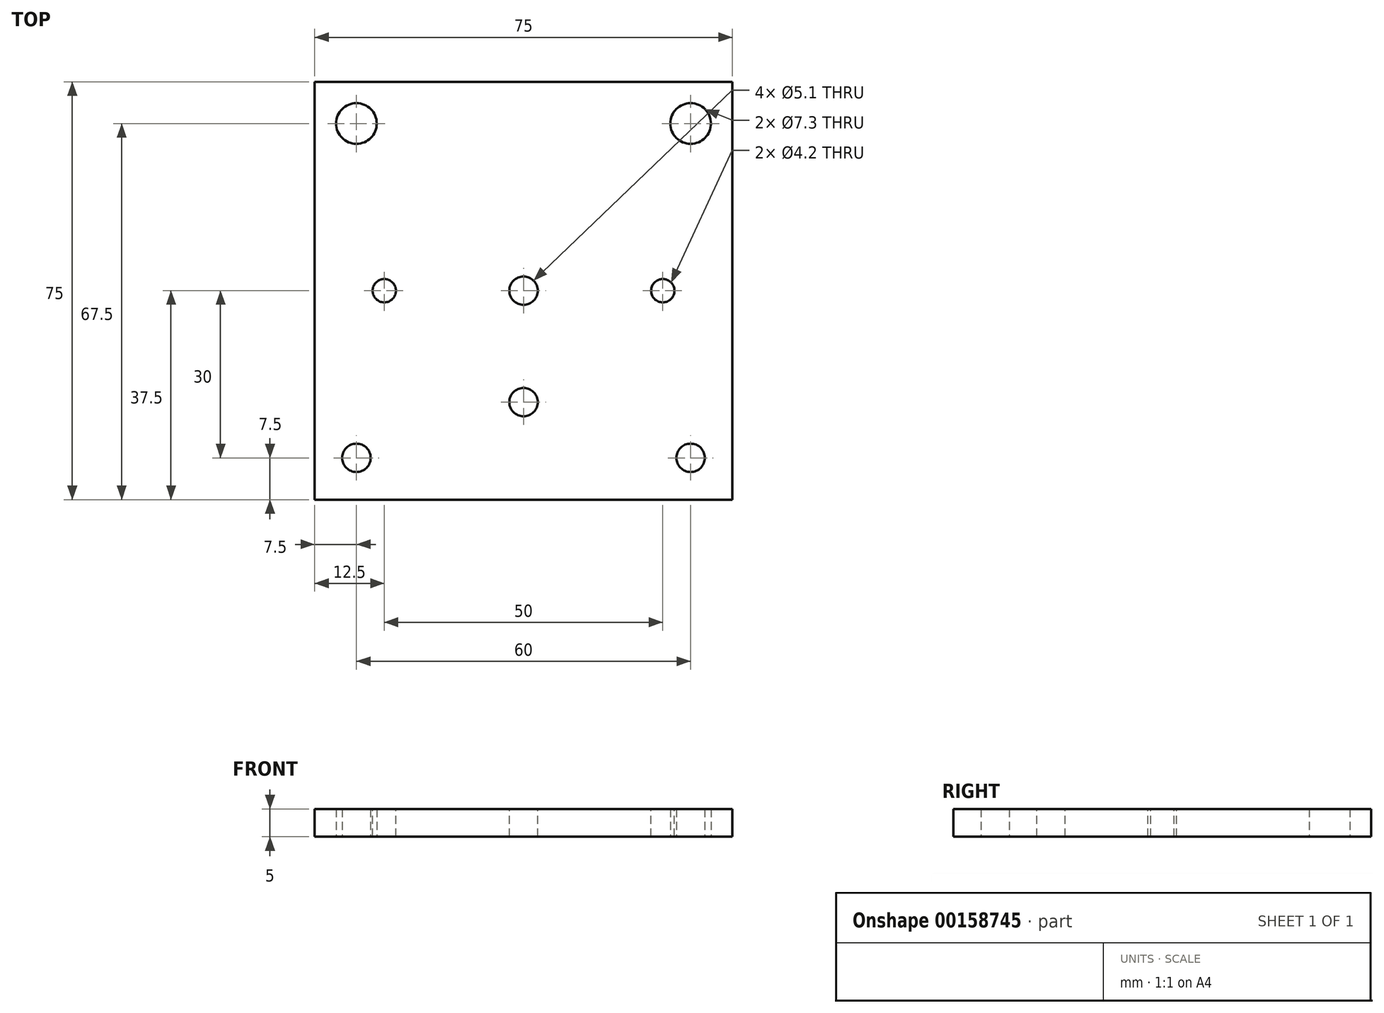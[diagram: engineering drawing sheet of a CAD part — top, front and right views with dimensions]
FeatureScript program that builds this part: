
annotation { "Feature Type Name" : "Feature", "Feature Type Description" : "" }
export const myFeature = defineFeature(function(context is Context, id is Id, definition is map)
    precondition{}
    {
        {
            var Q0;
            Q0=qCreatedBy(makeId("Top.planeOp"),FACE);
            var sketch = newSketch(context, id + "F3", { "sketchPlane" : qUnion([Q0])});
            skLineSegment(sketch, "E0.bottom", {"start": v(30, -30) * mm, "end": v(-30, -30) * mm});
            skLineSegment(sketch, "E0.top", {"start": v(30, 30) * mm, "end": v(-30, 30) * mm});
            skLineSegment(sketch, "E0.left", {"start": v(30, -30) * mm, "end": v(30, 30) * mm});
            skLineSegment(sketch, "E0.right", {"start": v(-30, -30) * mm, "end": v(-30, 30) * mm});
            skPoint(sketch, "E0.middle", {"position": v(0, 0) * mm});
            skLineSegment(sketch, "E1.bottom", {"start": v(37.5, -37.5) * mm, "end": v(-37.5, -37.5) * mm});
            skLineSegment(sketch, "E1.top", {"start": v(37.5, 37.5) * mm, "end": v(-37.5, 37.5) * mm});
            skLineSegment(sketch, "E1.left", {"start": v(37.5, -37.5) * mm, "end": v(37.5, 37.5) * mm});
            skLineSegment(sketch, "E1.right", {"start": v(-37.5, -37.5) * mm, "end": v(-37.5, 37.5) * mm});
            skSolve(sketch);
        }
        {
            var Q0;
            Q0=makeQuery(id+"F3.imprint","IMPRINT",FACE,{"disambiguationData":[TD([[makeQuery(id+"F3.imprint","IMPRINT",EDGE,{"derivedFrom":sQuery(id+"F3.wireOp",EDGE,"E0.bottom")}),-1.0]])]});
            var Q1;
            Q1=makeQuery(id+"F3.imprint","IMPRINT",FACE,{"disambiguationData":[TD([[makeQuery(id+"F3.imprint","IMPRINT",EDGE,{"derivedFrom":sQuery(id+"F3.wireOp",EDGE,"E0.bottom")}),1.0]])]});
            extrude(context, id + "F4", {"entities" : qUnion([Q0, Q1]), "depth" : 5 * mm});
        }
        {
            var Q0;
            Q0=sQuery(id+"F3.wireOp",VERTEX,"E0.bottom.end");
            var Q1;
            Q1=sQuery(id+"F3.wireOp",VERTEX,"E0.left.start");
            var Q2;
            Q2=makeQuery(id+"F4.opExtrude","SWEPT_BODY",BODY,{"disambiguationData":[OSD([sQuery(id+"F3.wireOp",EDGE,"E1.bottom"),sQuery(id+"F3.wireOp",EDGE,"E1.top"),sQuery(id+"F3.wireOp",EDGE,"E1.left"),sQuery(id+"F3.wireOp",EDGE,"E1.right")])]});
            hole(context, id + "F5", {"style" : HoleStyle.SIMPLE, "endStyle" : HoleEndStyle.THROUGH, "oppositeDirection" : true, "holeDiameter" : 5.1 * mm, "locations" : qUnion([Q0, Q1]), "scope" : qUnion([Q2]), "isTappedThrough" : true});
        }
        {
            var Q0;
            Q0=sQuery(id+"F3.wireOp",VERTEX,"E0.right.end");
            var Q1;
            Q1=sQuery(id+"F3.wireOp",VERTEX,"E0.left.end");
            var Q2;
            Q2=makeQuery(id+"F4.opExtrude","SWEPT_BODY",BODY,{"disambiguationData":[OSD([sQuery(id+"F3.wireOp",EDGE,"E1.bottom"),sQuery(id+"F3.wireOp",EDGE,"E1.top"),sQuery(id+"F3.wireOp",EDGE,"E1.left"),sQuery(id+"F3.wireOp",EDGE,"E1.right")])]});
            hole(context, id + "F0", {"style" : HoleStyle.SIMPLE, "endStyle" : HoleEndStyle.THROUGH, "oppositeDirection" : true, "holeDiameter" : 7.3 * mm, "locations" : qUnion([Q0, Q1]), "scope" : qUnion([Q2]), "isTappedThrough" : true});
        }
        {
            var Q0;
            Q0=makeQuery(id+"F4.opExtrude","CAP_FACE",FACE,{"disambiguationData":[OSD([sQuery(id+"F3.wireOp",EDGE,"E1.bottom"),sQuery(id+"F3.wireOp",EDGE,"E1.top"),sQuery(id+"F3.wireOp",EDGE,"E1.left"),sQuery(id+"F3.wireOp",EDGE,"E1.right")])],"isStart":false});
            var sketch = newSketch(context, id + "F6", { "sketchPlane" : qUnion([Q0])});
            skLineSegment(sketch, "E2", {"start": v(0, 0) * mm, "end": v(0, -20) * mm});
            skSolve(sketch);
        }
        {
            var Q0;
            Q0=sQuery(id+"F6.wireOp",VERTEX,"E2.start");
            var Q1;
            Q1=sQuery(id+"F6.wireOp",VERTEX,"E2.end");
            var Q2;
            Q2=makeQuery(id+"F4.opExtrude","SWEPT_BODY",BODY,{"disambiguationData":[OSD([sQuery(id+"F3.wireOp",EDGE,"E1.bottom"),sQuery(id+"F3.wireOp",EDGE,"E1.top"),sQuery(id+"F3.wireOp",EDGE,"E1.left"),sQuery(id+"F3.wireOp",EDGE,"E1.right")])]});
            hole(context, id + "F1", {"style" : HoleStyle.SIMPLE, "endStyle" : HoleEndStyle.THROUGH, "holeDiameter" : 5.1 * mm, "locations" : qUnion([Q0, Q1]), "scope" : qUnion([Q2]), "isTappedThrough" : true});
        }
        {
            var Q0;
            Q0=makeQuery(id+"F4.opExtrude","CAP_FACE",FACE,{"disambiguationData":[OSD([sQuery(id+"F3.wireOp",EDGE,"E1.bottom"),sQuery(id+"F3.wireOp",EDGE,"E1.top"),sQuery(id+"F3.wireOp",EDGE,"E1.left"),sQuery(id+"F3.wireOp",EDGE,"E1.right")])],"isStart":false});
            var sketch = newSketch(context, id + "F2", { "sketchPlane" : qUnion([Q0])});
            skPoint(sketch, "E3", {"position": v(-25, 0) * mm});
            skPoint(sketch, "E4", {"position": v(25, 0) * mm});
            skSolve(sketch);
        }
        {
            var Q0;
            Q0=sQuery(id+"F2.wireOp",VERTEX,"E4");
            var Q1;
            Q1=sQuery(id+"F2.wireOp",VERTEX,"E3");
            var Q2;
            Q2=makeQuery(id+"F4.opExtrude","SWEPT_BODY",BODY,{"disambiguationData":[OSD([sQuery(id+"F3.wireOp",EDGE,"E1.bottom"),sQuery(id+"F3.wireOp",EDGE,"E1.top"),sQuery(id+"F3.wireOp",EDGE,"E1.left"),sQuery(id+"F3.wireOp",EDGE,"E1.right")])]});
            hole(context, id + "F7", {"style" : HoleStyle.SIMPLE, "endStyle" : HoleEndStyle.THROUGH, "holeDiameter" : 4.2 * mm, "locations" : qUnion([Q0, Q1]), "scope" : qUnion([Q2]), "isTappedThrough" : true});
        }
    });
